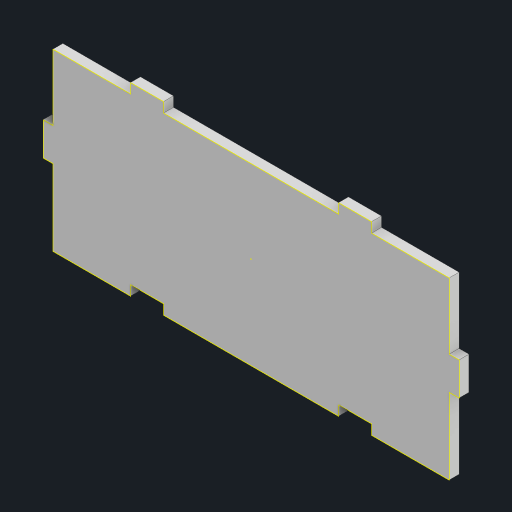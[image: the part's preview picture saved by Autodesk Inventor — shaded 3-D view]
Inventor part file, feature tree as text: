
AUTODESK INVENTOR PART (.ipt)
format: ipt  version: 2023 (Build 270158000, 158)  size: 217,088 bytes
history: native  units: mm
features: reference x21, sketch x6, other x6, extrude x5, projected_geometry x1
ambient origin geometry x8: Origin, YZ Plane, XZ Plane, XY Plane, X Axis, Y Axis, Z Axis, Center Point
bodies: Solid1 (feature_tree)
feature tree (39):
  extrude  "Extrusion1"  Depth=50.0mm
  extrude  "Extrusion2"  Depth=3.0mm TaperAngle=0.0deg
  extrude  "Extrusion5"  Depth=10.0mm
  extrude  "Extrusion6"  Depth=10.0mm
  extrude  "Extrusion7"  Depth=126.0mm
  sketch  "Sketch7"  dims[d24=31.5mm d25=3.0mm d26=0.0mm d27=3.0mm d28=0.0mm d29=23.0mm d30=3.0mm d31=10.0mm d32=23.0mm d33=3.0mm d34=10.0mm d35=0.0mm d36=0.0mm d37=0.5mm d38=0.872665mm]
  sketch  "Sketch1"  dims[d0=120.0mm d1=50.0mm]
  sketch  "Sketch2"  dims[d2=3.0mm d3=0.0mm d4=3.0mm d5=0.0mm]
  reference  "Reference1"
  reference  "Reference2"
  reference  "Reference3"
  reference  "Reference4"
  reference  "Reference5"
  reference  "Reference6"
  reference  "Reference7"
  reference  "Reference8"
  reference  "Reference9"
  reference  "Reference10"
  reference  "Reference11"
  reference  "Reference12"
  reference  "Reference13"
  reference  "Reference14"
  reference  "Reference15"
  reference  "Reference16"
  reference  "Reference17"
  reference  "Reference18"
  reference  "Reference19"
  sketch  "Sketch4"  dims[d10=126.0mm d11=31.5mm d18=10.0mm]
  sketch  "Sketch5"  dims[d19=3.0mm d20=10.0mm d21=3.0mm]
  reference  "Reference20"
  sketch  "Sketch6"  dims[d22=126.0mm d23=31.5mm]
  reference  "Reference21"
  parser-record x1  (decoder bookkeeping rows leaked as tree rows — omitted from the tree; the rows remain in map.json)
  other  "AlarmClock.iam"
  other  "Bottom:1"
  other  "left:1"
  other  "right:1"
  other  "top:1"
  projected_geometry  "Project Cut Edges1"
note: 1 file-system path scrubbed to <path> (originals preserved in map.json)
